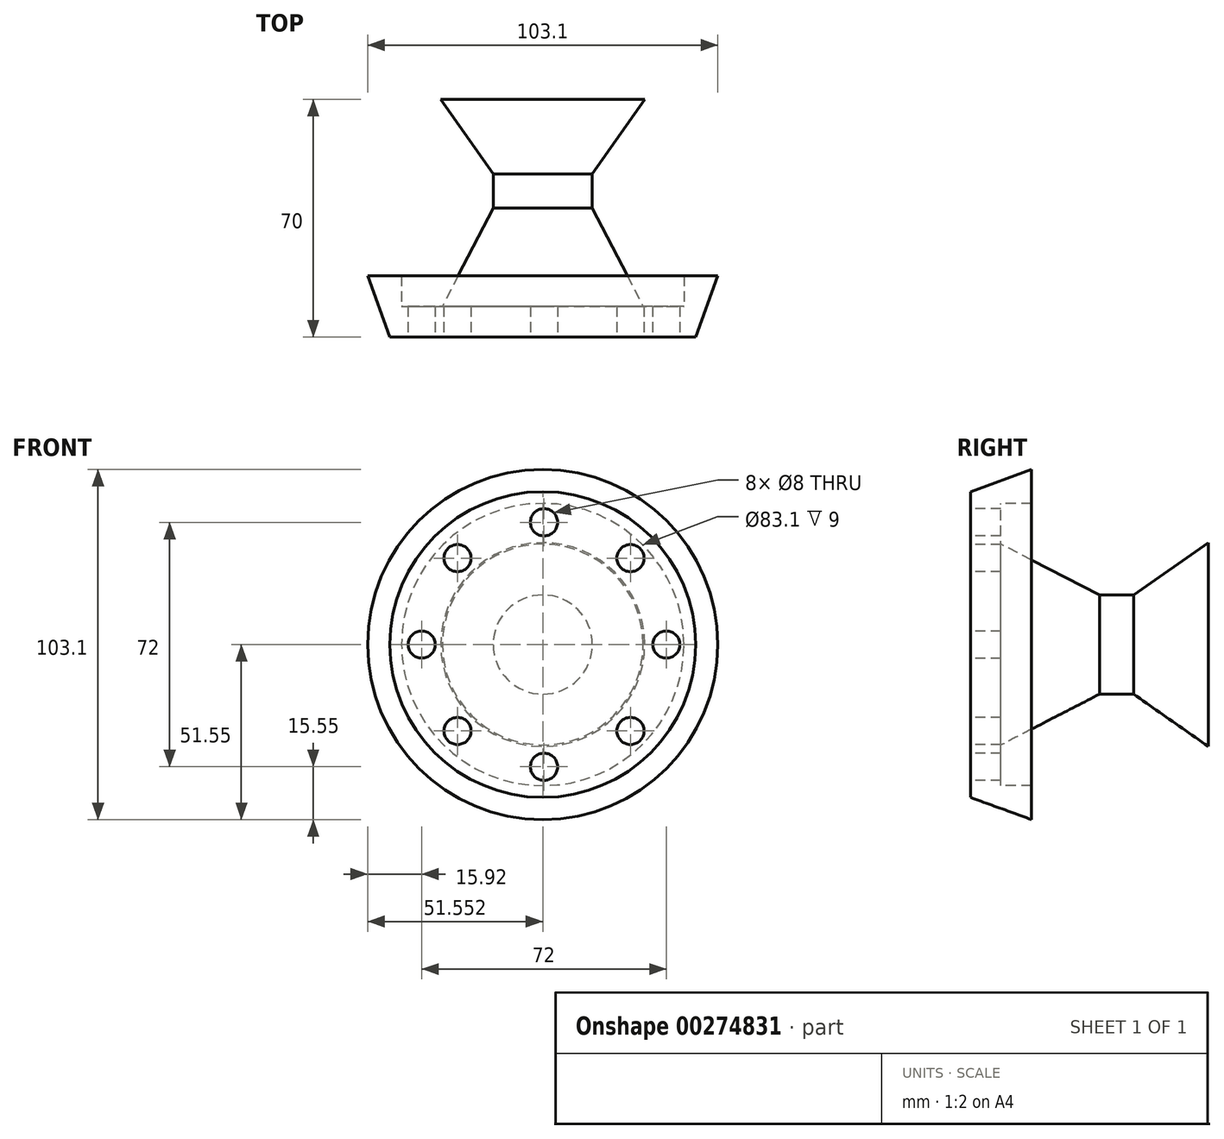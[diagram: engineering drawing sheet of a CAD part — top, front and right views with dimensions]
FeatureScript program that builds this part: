
annotation { "Feature Type Name" : "Feature", "Feature Type Description" : "" }
export const myFeature = defineFeature(function(context is Context, id is Id, definition is map)
    precondition{}
    {
        {
            var Q0;
            Q0=qCreatedBy(makeId("Top.planeOp"),FACE);
            var sketch = newSketch(context, id + "F0", { "sketchPlane" : qUnion([Q0])});
            skLineSegment(sketch, "E0", {"start": v(-0.37, 0.1) * mm, "end": v(-0.37, 70.1) * mm});
            skLineSegment(sketch, "E1", {"start": v(-0.37, 70.1) * mm, "end": v(-30.37, 70.1) * mm});
            skLineSegment(sketch, "E2", {"start": v(-30.37, 70.1) * mm, "end": v(-14.96, 48.1) * mm});
            skLineSegment(sketch, "E3", {"start": v(-14.96, 48.1) * mm, "end": v(-14.96, 38.1) * mm});
            skLineSegment(sketch, "E4", {"start": v(-14.96, 38.1) * mm, "end": v(-29.92, 9.1) * mm});
            skLineSegment(sketch, "E5", {"start": v(-29.92, 9.1) * mm, "end": v(-41.92, 9.1) * mm});
            skLineSegment(sketch, "E6", {"start": v(-41.92, 9.1) * mm, "end": v(-41.92, 18.1) * mm});
            skLineSegment(sketch, "E7", {"start": v(-41.92, 18.1) * mm, "end": v(-51.92, 18.1) * mm});
            skLineSegment(sketch, "E8", {"start": v(-51.92, 18.1) * mm, "end": v(-45.37, 0.1) * mm});
            skLineSegment(sketch, "E9", {"start": v(-45.37, 0.1) * mm, "end": v(-0.37, 0.1) * mm});
            skSolve(sketch);
        }
        {
            var Q0;
            Q0=makeQuery(id+"F0.imprint","IMPRINT",FACE,{"disambiguationData":[TD([[makeQuery(id+"F0.imprint","IMPRINT",EDGE,{"derivedFrom":sQuery(id+"F0.wireOp",EDGE,"E0")}),1.0]])]});
            var Q1;
            Q1=sQuery(id+"F0.wireOp",EDGE,"E0");
            revolve(context, id + "F1", {"entities" : qUnion([Q0]), "axis" : qUnion([Q1]), "revolveType" : RevolveType.FULL});
        }
        {
            var Q0;
            Q0=makeQuery(id+"F1.opRevolve","SWEPT_FACE",FACE,{"disambiguationData":[OSD([sQuery(id+"F0.wireOp",EDGE,"E9")])]});
            var sketch = newSketch(context, id + "F2", { "sketchPlane" : qUnion([Q0])});
            skCircle(sketch, "E10", {"center": v(-36, 0) * mm, "radius": 4 * mm});
            skCircle(sketch, "E11.1.0", {"center": v(-25.46, -25.46) * mm, "radius": 4 * mm});
            skCircle(sketch, "E11.2.0", {"center": v(0, -36) * mm, "radius": 4 * mm});
            skCircle(sketch, "E11.3.0", {"center": v(25.46, -25.46) * mm, "radius": 4 * mm});
            skCircle(sketch, "E11.4.0", {"center": v(36, 0) * mm, "radius": 4 * mm});
            skCircle(sketch, "E11.5.0", {"center": v(25.46, 25.46) * mm, "radius": 4 * mm});
            skCircle(sketch, "E11.6.0", {"center": v(0, 36) * mm, "radius": 4 * mm});
            skCircle(sketch, "E11.7.0", {"center": v(-25.46, 25.46) * mm, "radius": 4 * mm});
            skPoint(sketch, "E11.center", {"position": v(0, 0) * mm});
            skSolve(sketch);
        }
        {
            var Q0;
            Q0 = qSketchRegion(id + "F2", true);
            extrude(context, id + "F3", {"entities" : qUnion([Q0]), "operationType" : NewBodyOperationType.REMOVE, "endBound" : BoundingType.UP_TO_NEXT, "oppositeDirection" : true, "depth" : 25 * mm});
        }
    });
